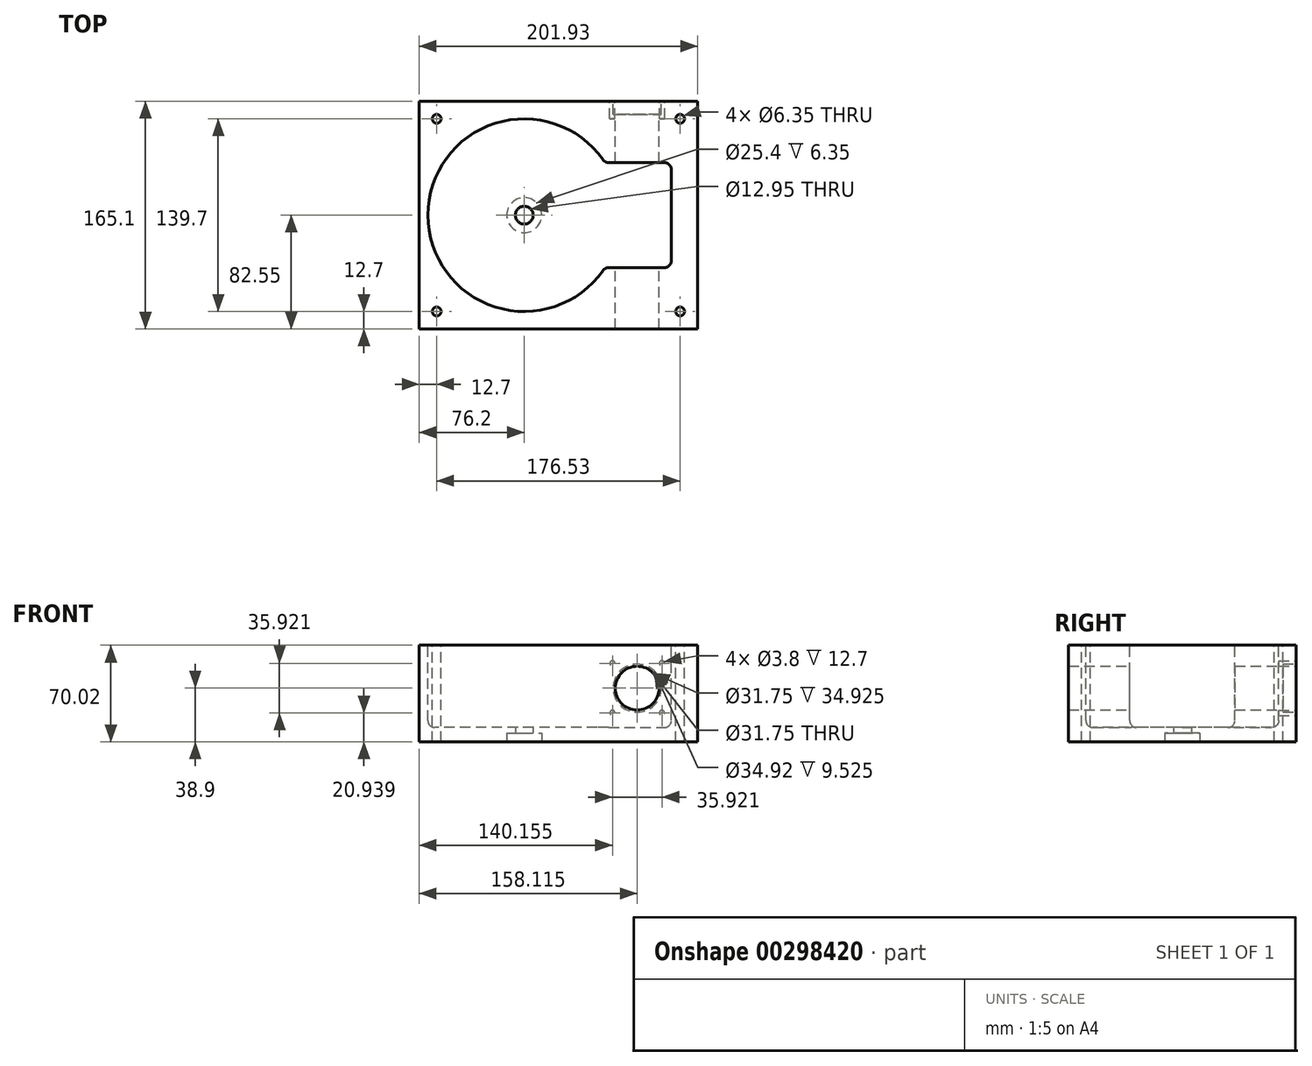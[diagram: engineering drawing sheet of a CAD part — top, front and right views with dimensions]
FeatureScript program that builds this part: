
annotation { "Feature Type Name" : "Feature", "Feature Type Description" : "" }
export const myFeature = defineFeature(function(context is Context, id is Id, definition is map)
    precondition{}
    {
        {
            var Q0;
            Q0=qCreatedBy(makeId("Top.planeOp"),FACE);
            var sketch = newSketch(context, id + "F0", { "sketchPlane" : qUnion([Q0])});
            skCircle(sketch, "E0", {"center": v(0, 0) * mm, "radius": 63.5 * mm});
            skSolve(sketch);
        }
        {
            var Q0;
            Q0=qCreatedBy(makeId("Front.planeOp"),FACE);
            var sketch = newSketch(context, id + "F1", { "sketchPlane" : qUnion([Q0])});
            skCircle(sketch, "E1", {"center": v(81.92, 0) * mm, "radius": 18.41 * mm});
            skLineSegment(sketch, "E2.bottom", {"start": v(-63.5, 7.94) * mm, "end": v(63.5, 7.94) * mm});
            skLineSegment(sketch, "E2.top", {"start": v(-63.5, -7.95) * mm, "end": v(-24.64, -7.95) * mm});
            skLineSegment(sketch, "E2.left", {"start": v(-63.5, 7.94) * mm, "end": v(-63.5, -7.95) * mm});
            skLineSegment(sketch, "E2.right", {"start": v(63.5, 7.94) * mm, "end": v(63.5, -7.95) * mm});
            skLineSegment(sketch, "E3", {"start": v(24.64, -27) * mm, "end": v(24.64, -7.95) * mm});
            skLineSegment(sketch, "E4", {"start": v(-24.64, -27) * mm, "end": v(-24.64, -7.95) * mm});
            skLineSegment(sketch, "E5", {"start": v(-24.64, -27) * mm, "end": v(24.64, -27) * mm});
            skLineSegment(sketch, "E6.trimOffspring", {"start": v(24.64, -7.95) * mm, "end": v(63.5, -7.95) * mm});
            skLineSegment(sketch, "E7.bottom", {"start": v(12.7, -29.38) * mm, "end": v(-12.7, -29.38) * mm});
            skLineSegment(sketch, "E7.top", {"start": v(12.7, -27) * mm, "end": v(-12.7, -27) * mm});
            skLineSegment(sketch, "E7.left", {"start": v(12.7, -29.38) * mm, "end": v(12.7, -27) * mm});
            skLineSegment(sketch, "E7.right", {"start": v(-12.7, -29.38) * mm, "end": v(-12.7, -27) * mm});
            skLineSegment(sketch, "E8", {"start": v(0, 0) * mm, "end": v(0, -58.85) * mm, "construction": true});
            skPoint(sketch, "E8.endSnap0", {"position": v(0, -27) * mm});
            skSolve(sketch);
        }
        {
            var Q0;
            Q0=qCreatedBy(makeId("Front.planeOp"),FACE);
            var sketch = newSketch(context, id + "F2", { "sketchPlane" : qUnion([Q0])});
            skLineSegment(sketch, "E9.bottom", {"start": v(-76.2, 31.11) * mm, "end": v(125.73, 31.12) * mm});
            skLineSegment(sketch, "E9.top", {"start": v(-76.2, -38.9) * mm, "end": v(125.73, -38.9) * mm});
            skLineSegment(sketch, "E9.left", {"start": v(-76.2, 31.11) * mm, "end": v(-76.2, -38.9) * mm});
            skLineSegment(sketch, "E9.right", {"start": v(125.73, 31.12) * mm, "end": v(125.73, -38.9) * mm});
            skSolve(sketch);
        }
        {
            var Q0;
            Q0=makeQuery(id+"F2.imprint","IMPRINT",FACE,{"disambiguationData":[TD([[makeQuery(id+"F2.imprint","IMPRINT",EDGE,{"derivedFrom":sQuery(id+"F2.wireOp",EDGE,"E9.bottom")}),-1.0]])]});
            extrude(context, id + "F3", {"entities" : qUnion([Q0]), "depth" : 165.1 * mm, "symmetric" : true});
        }
        {
            var Q0;
            Q0=makeQuery(id+"F3.opExtrude","SWEPT_FACE",FACE,{"disambiguationData":[OSD([sQuery(id+"F2.wireOp",EDGE,"E9.bottom")])]});
            var sketch = newSketch(context, id + "F4", { "sketchPlane" : qUnion([Q0])});
            skArc(sketch, "E10.0", {"start": v(58.54, 38.1) * mm, "mid": v(-69.85, 0) * mm, "end": v(58.54, -38.1) * mm});
            skLineSegment(sketch, "E11.bottom", {"start": v(58.54, 38.1) * mm, "end": v(106.68, 38.1) * mm});
            skLineSegment(sketch, "E11.top", {"start": v(58.54, -38.1) * mm, "end": v(106.68, -38.1) * mm});
            skLineSegment(sketch, "E11.right", {"start": v(106.68, 38.1) * mm, "end": v(106.68, -38.1) * mm});
            skLineSegment(sketch, "E12", {"start": v(106.68, 0) * mm, "end": v(125.73, 0) * mm, "construction": true});
            skSolve(sketch);
        }
        {
            var Q0;
            Q0 = qSketchRegion(id + "F4", true);
            extrude(context, id + "F5", {"entities" : qUnion([Q0]), "operationType" : NewBodyOperationType.REMOVE, "oppositeDirection" : true, "depth" : 59.7 * mm});
        }
        {
            var Q0;
            Q0=makeQuery(id+"F3.opExtrude","SWEPT_FACE",FACE,{"disambiguationData":[OSD([sQuery(id+"F2.wireOp",EDGE,"E9.top")])]});
            var sketch = newSketch(context, id + "F6", { "sketchPlane" : qUnion([Q0])});
            skCircle(sketch, "E13", {"center": v(0, 0) * mm, "radius": 12.7 * mm});
            skSolve(sketch);
        }
        {
            var Q0;
            Q0=makeQuery(id+"F6.imprint","IMPRINT",FACE,{"disambiguationData":[TD([[makeQuery(id+"F6.imprint","IMPRINT",EDGE,{"derivedFrom":sQuery(id+"F6.wireOp",EDGE,"E13")}),1.0]])]});
            extrude(context, id + "F7", {"entities" : qUnion([Q0]), "operationType" : NewBodyOperationType.REMOVE, "oppositeDirection" : true, "depth" : 6.35 * mm});
        }
        {
            var Q0;
            Q0=makeQuery(id+"F7.boolean.opBoolean","COPY",FACE,{"derivedFrom":makeQuery(id+"F7.opExtrude","CAP_FACE",FACE,{"disambiguationData":[OSD([sQuery(id+"F6.wireOp",EDGE,"E13")])],"isStart":false})});
            var sketch = newSketch(context, id + "F8", { "sketchPlane" : qUnion([Q0])});
            skCircle(sketch, "E14", {"center": v(0, 0) * mm, "radius": 6.48 * mm});
            skSolve(sketch);
        }
        {
            var Q0;
            Q0 = qSketchRegion(id + "F8", true);
            extrude(context, id + "F9", {"entities" : qUnion([Q0]), "operationType" : NewBodyOperationType.REMOVE, "oppositeDirection" : true, "depth" : 25.4 * mm});
        }
        {
            var Q0;
            Q0=makeQuery(id+"F3.opExtrude","CAP_FACE",FACE,{"disambiguationData":[OSD([sQuery(id+"F2.wireOp",EDGE,"E9.bottom"),sQuery(id+"F2.wireOp",EDGE,"E9.top"),sQuery(id+"F2.wireOp",EDGE,"E9.left"),sQuery(id+"F2.wireOp",EDGE,"E9.right")])],"isStart":true});
            var sketch = newSketch(context, id + "F10", { "sketchPlane" : qUnion([Q0])});
            skCircle(sketch, "E15", {"center": v(-81.92, 0) * mm, "radius": 15.88 * mm});
            skSolve(sketch);
        }
        {
            var Q0;
            Q0=makeQuery(id+"F10.imprint","IMPRINT",FACE,{"disambiguationData":[TD([[makeQuery(id+"F10.imprint","IMPRINT",EDGE,{"derivedFrom":sQuery(id+"F10.wireOp",EDGE,"E15")}),1.0]])]});
            extrude(context, id + "F11", {"entities" : qUnion([Q0]), "operationType" : NewBodyOperationType.REMOVE, "endBound" : BoundingType.THROUGH_ALL, "oppositeDirection" : true, "depth" : 152.4 * mm});
        }
        {
            var Q0;
            Q0=makeQuery(id+"F3.opExtrude","SWEPT_FACE",FACE,{"disambiguationData":[OSD([sQuery(id+"F2.wireOp",EDGE,"E9.bottom")])]});
            var sketch = newSketch(context, id + "F12", { "sketchPlane" : qUnion([Q0])});
            skCircle(sketch, "E16", {"center": v(-63.5, 69.85) * mm, "radius": 3.18 * mm});
            skCircle(sketch, "E17.0.1.0", {"center": v(-63.5, -69.85) * mm, "radius": 3.18 * mm});
            skCircle(sketch, "E17.1.0.0", {"center": v(113.03, 69.85) * mm, "radius": 3.18 * mm});
            skCircle(sketch, "E17.1.1.0", {"center": v(113.03, -69.85) * mm, "radius": 3.18 * mm});
            skLineSegment(sketch, "E17.direction1", {"start": v(-63.5, 69.85) * mm, "end": v(113.03, 69.85) * mm, "construction": true});
            skLineSegment(sketch, "E17.direction2", {"start": v(-63.5, 69.85) * mm, "end": v(-63.5, -69.85) * mm, "construction": true});
            skSolve(sketch);
        }
        {
            var Q0;
            Q0 = qSketchRegion(id + "F12", true);
            extrude(context, id + "F13", {"entities" : qUnion([Q0]), "operationType" : NewBodyOperationType.REMOVE, "endBound" : BoundingType.THROUGH_ALL, "oppositeDirection" : true, "depth" : 25.4 * mm});
        }
        {
            var Q0;
            Q0=makeQuery(id+"F3.opExtrude","CAP_FACE",FACE,{"disambiguationData":[OSD([sQuery(id+"F2.wireOp",EDGE,"E9.bottom"),sQuery(id+"F2.wireOp",EDGE,"E9.top"),sQuery(id+"F2.wireOp",EDGE,"E9.left"),sQuery(id+"F2.wireOp",EDGE,"E9.right")])],"isStart":true});
            var sketch = newSketch(context, id + "F14", { "sketchPlane" : qUnion([Q0])});
            skCircle(sketch, "E18", {"center": v(-81.92, 0) * mm, "radius": 17.46 * mm});
            skSolve(sketch);
        }
        {
            var Q0;
            Q0=makeQuery(id+"F3.opExtrude","CAP_FACE",FACE,{"disambiguationData":[OSD([sQuery(id+"F2.wireOp",EDGE,"E9.bottom"),sQuery(id+"F2.wireOp",EDGE,"E9.top"),sQuery(id+"F2.wireOp",EDGE,"E9.left"),sQuery(id+"F2.wireOp",EDGE,"E9.right")])],"isStart":true});
            var sketch = newSketch(context, id + "F15", { "sketchPlane" : qUnion([Q0])});
            skCircle(sketch, "E19", {"center": v(-99.88, 17.96) * mm, "radius": 1.9 * mm});
            skCircle(sketch, "E20", {"center": v(-81.92, 0) * mm, "radius": 25.4 * mm, "construction": true});
            skLineSegment(sketch, "E21", {"start": v(-99.88, 17.96) * mm, "end": v(-81.92, 0) * mm, "construction": true});
            skCircle(sketch, "E22.1.0", {"center": v(-99.88, -17.96) * mm, "radius": 1.9 * mm});
            skCircle(sketch, "E22.2.0", {"center": v(-63.95, -17.96) * mm, "radius": 1.9 * mm});
            skCircle(sketch, "E22.3.0", {"center": v(-63.95, 17.96) * mm, "radius": 1.9 * mm});
            skSolve(sketch);
        }
        {
            var Q0;
            Q0 = qSketchRegion(id + "F15", true);
            extrude(context, id + "F16", {"entities" : qUnion([Q0]), "operationType" : NewBodyOperationType.REMOVE, "oppositeDirection" : true, "depth" : 12.7 * mm});
        }
        {
            var Q0;
            Q0 = qSketchRegion(id + "F14", true);
            extrude(context, id + "F17", {"entities" : qUnion([Q0]), "operationType" : NewBodyOperationType.REMOVE, "oppositeDirection" : true, "depth" : 9.52 * mm});
        }
        {
            var Q0;
            Q0=makeQuery(id+"F5.boolean.opBoolean","COPY",EDGE,{"derivedFrom":makeQuery(id+"F5.opExtrude","CAP_EDGE",EDGE,{"disambiguationData":[OSD([sQuery(id+"F4.wireOp",EDGE,"E10.0")])],"isStart":false})});
            var Q1;
            Q1=makeQuery(id+"F5.boolean.opBoolean","COPY",EDGE,{"derivedFrom":makeQuery(id+"F5.opExtrude","CAP_EDGE",EDGE,{"disambiguationData":[OSD([sQuery(id+"F4.wireOp",EDGE,"E11.bottom")])],"isStart":false})});
            var Q2;
            Q2=makeQuery(id+"F5.boolean.opBoolean","COPY",EDGE,{"derivedFrom":makeQuery(id+"F5.opExtrude","CAP_EDGE",EDGE,{"disambiguationData":[OSD([sQuery(id+"F4.wireOp",EDGE,"E11.right")])],"isStart":false})});
            var Q3;
            Q3=makeQuery(id+"F5.boolean.opBoolean","COPY",EDGE,{"derivedFrom":makeQuery(id+"F5.opExtrude","CAP_EDGE",EDGE,{"disambiguationData":[OSD([sQuery(id+"F4.wireOp",EDGE,"E11.top")])],"isStart":false})});
            var Q4;
            Q4=makeQuery(id+"F5.boolean.opBoolean","COPY",EDGE,{"derivedFrom":makeQuery(id+"F5.opExtrude","SWEPT_EDGE",EDGE,{"disambiguationData":[OSD([sQuery(id+"F4.wireOp",EDGE,"E10.0"),sQuery(id+"F4.wireOp",EDGE,"E11.bottom")])]})});
            var Q5;
            Q5=makeQuery(id+"F5.boolean.opBoolean","COPY",EDGE,{"derivedFrom":makeQuery(id+"F5.opExtrude","SWEPT_EDGE",EDGE,{"disambiguationData":[OSD([sQuery(id+"F4.wireOp",EDGE,"E10.0"),sQuery(id+"F4.wireOp",EDGE,"E11.top")])]})});
            var Q6;
            Q6=makeQuery(id+"F5.boolean.opBoolean","COPY",EDGE,{"derivedFrom":makeQuery(id+"F5.opExtrude","SWEPT_EDGE",EDGE,{"disambiguationData":[OSD([sQuery(id+"F4.wireOp",EDGE,"E11.bottom"),sQuery(id+"F4.wireOp",EDGE,"E11.right")])]})});
            var Q7;
            Q7=makeQuery(id+"F5.boolean.opBoolean","COPY",EDGE,{"derivedFrom":makeQuery(id+"F5.opExtrude","SWEPT_EDGE",EDGE,{"disambiguationData":[OSD([sQuery(id+"F4.wireOp",EDGE,"E11.top"),sQuery(id+"F4.wireOp",EDGE,"E11.right")])]})});
            fillet(context, id + "F18", {"entities" : qUnion([Q0, Q1, Q2, Q3, Q4, Q5, Q6, Q7]), "radius" : 5.08 * mm, "tangentPropagation" : true, "allowEdgeOverflow" : false});
        }
    });
